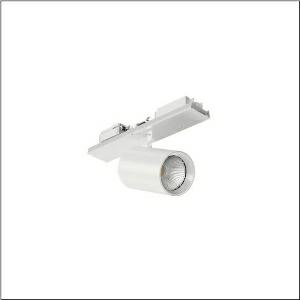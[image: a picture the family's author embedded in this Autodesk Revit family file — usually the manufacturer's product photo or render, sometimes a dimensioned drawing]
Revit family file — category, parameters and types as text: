
# Revit family: licross_spot_31_51sl14da43b
name_source: partatom
category: Lighting Fixtures
units: mm (PartAtom-declared; Revit-internal decimal feet)

## family parameters
Cut with Voids When Loaded = No
Host = Face
Light Source = No
Part Type = Normal
Room Calculation Point = No
Round Connector Dimension = Use Diameter
Shared = No

## types (1)
- --- (1 x LED, 3720 lm, 28.5 W, 4000K)
    Apparent Load = 29 VA
    CIE Flux Codes = 93 97 100 100 100
    Color Rendering = 90
    Color Temperature = 4000K
    Default Elevation = 1800 mm
    Description = Licross Spot 31, directional spotlight, light control with lens, of plastic, LED rated luminous flux: 3.720lm, light colour: 940, with plug, 5-pole, mains connection: 220..240V, AC, 50/60Hz, of aluminium, traffic white (RAL 9016), length: 300mm, diameter: 90mm, protection rating (complete): IP20, insulation class (complete): insulation class I (protective earthing), certification: CE, packaging unit: 1 piece
    Height = 175 mm
    Lamp = 1 x LED
    Lamp Light Flux = 3720 lm
    Lamp Power = 28.5 W
    Lamp count = 1
    Length = 90 mm
    Luminous efficacy = 131 lm/W
    Manufacturer = Siteco
    ModVariant = No
    Model = 51SL14DA43B
    Mounting Place = Ceiling
    Mounting Type = Pendant
    Number of Poles = 1
    OnlyDefault = Yes
    Power Factor = 1
    Product Name = Licross Spot 31
    Product group = directional spotlight
    ProductGroupID = 905
    Protection Class = Protection class I
    Protection Degree = IP 20
    RLX_Detail_Level = 1
    RLX_Emergency_Light_Flux = 0 lm
    RLX_Emergency_Type = 0
    RLX_Emergency_Type_DB = No
    RlxData = <blob elided: 14785 chars, md5=baeddba1>
    Socket = socket
    Standby Power = 0 W
    System Light Flux = 3720 lm
    System Power = 29 W
    Type Comments = factory setting: luminous flux: 100 % | (ON | ON | ON) | 700 mA
    Type Image = l_1245720.jpg
    URL = http://relux.com
    VarID = @adj_131385
    Voltage = 0 V
    Weight = 0.00 kg
    Width = 0 mm  [stored 0 ft]

note: [stored X ft] marks values corroborated as IEEE doubles in the binary element streams (Revit-internal decimal feet)

## geometry (parser evidence)
native form markers: Sweep x11
no freeform markers — native parametric forms only
